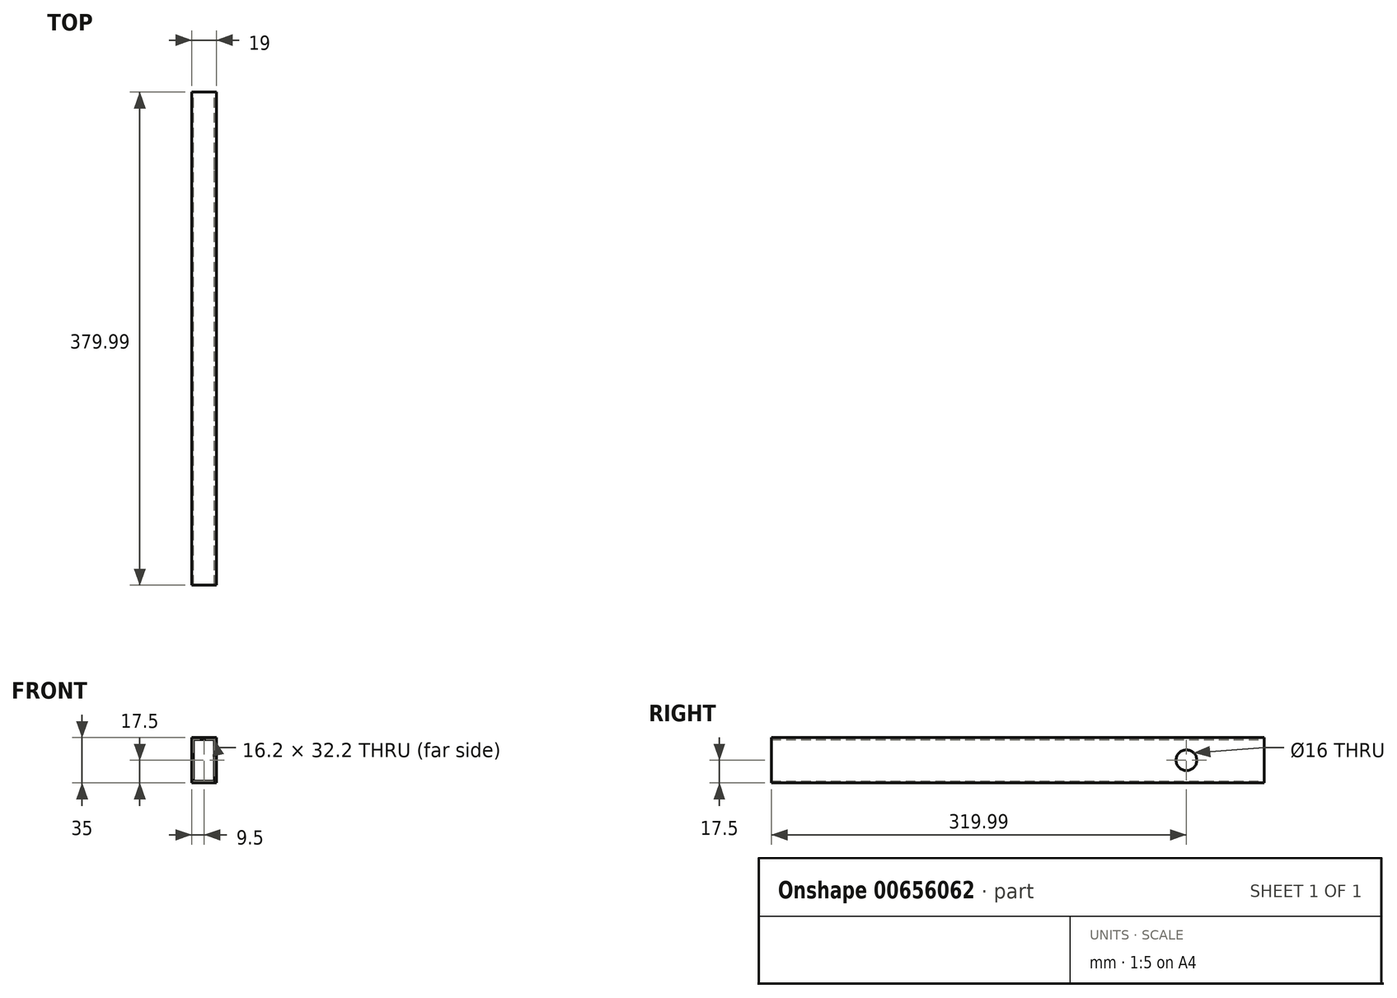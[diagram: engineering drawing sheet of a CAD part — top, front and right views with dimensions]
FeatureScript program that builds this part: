
annotation { "Feature Type Name" : "Feature", "Feature Type Description" : "" }
export const myFeature = defineFeature(function(context is Context, id is Id, definition is map)
    precondition{}
    {
        {
            var Q0;
            Q0=qCreatedBy(makeId("Front.planeOp"),FACE);
            var sketch = newSketch(context, id + "F0", { "sketchPlane" : qUnion([Q0])});
            skLineSegment(sketch, "E0.bottom", {"start": v(0, 0) * mm, "end": v(19, 0) * mm});
            skLineSegment(sketch, "E0.top", {"start": v(0, -35) * mm, "end": v(19, -35) * mm});
            skLineSegment(sketch, "E0.left", {"start": v(0, 0) * mm, "end": v(0, -35) * mm});
            skLineSegment(sketch, "E0.right", {"start": v(19, 0) * mm, "end": v(19, -35) * mm});
            skLineSegment(sketch, "E1.0", {"start": v(1.4, -1.4) * mm, "end": v(17.6, -1.4) * mm});
            skLineSegment(sketch, "E1.1", {"start": v(1.4, -1.4) * mm, "end": v(1.4, -33.6) * mm});
            skLineSegment(sketch, "E1.2", {"start": v(1.4, -33.6) * mm, "end": v(17.6, -33.6) * mm});
            skLineSegment(sketch, "E1.3", {"start": v(17.6, -1.4) * mm, "end": v(17.6, -33.6) * mm});
            skSolve(sketch);
        }
        {
            var Q0;
            Q0=makeQuery(id+"F0.imprint","IMPRINT",FACE,{"disambiguationData":[TD([[makeQuery(id+"F0.imprint","IMPRINT",EDGE,{"derivedFrom":sQuery(id+"F0.wireOp",EDGE,"E0.bottom")}),-1.0]])]});
            extrude(context, id + "F1", {"entities" : qUnion([Q0]), "depth" : 475 * mm + 60 * mm - 5 * mm - 150 * mm, "offsetDistance" : 25.4 * mm});
        }
        {
            var Q0;
            Q0=makeQuery(id+"F1.opExtrude","SWEPT_FACE",FACE,{"disambiguationData":[OSD([sQuery(id+"F0.wireOp",EDGE,"E0.right")])]});
            var sketch = newSketch(context, id + "F2", { "sketchPlane" : qUnion([Q0])});
            skCircle(sketch, "E2", {"center": v(-60, -17.5) * mm, "radius": 8 * mm});
            skSolve(sketch);
        }
        {
            var Q0;
            Q0=makeQuery(id+"F2.imprint","IMPRINT",FACE,{"disambiguationData":[TD([[makeQuery(id+"F2.imprint","IMPRINT",EDGE,{"derivedFrom":sQuery(id+"F2.wireOp",EDGE,"E2")}),1.0]])]});
            extrude(context, id + "F3", {"entities" : qUnion([Q0]), "operationType" : NewBodyOperationType.REMOVE, "oppositeDirection" : true, "depth" : 15 * mm, "offsetDistance" : 25.4 * mm});
        }
    });
